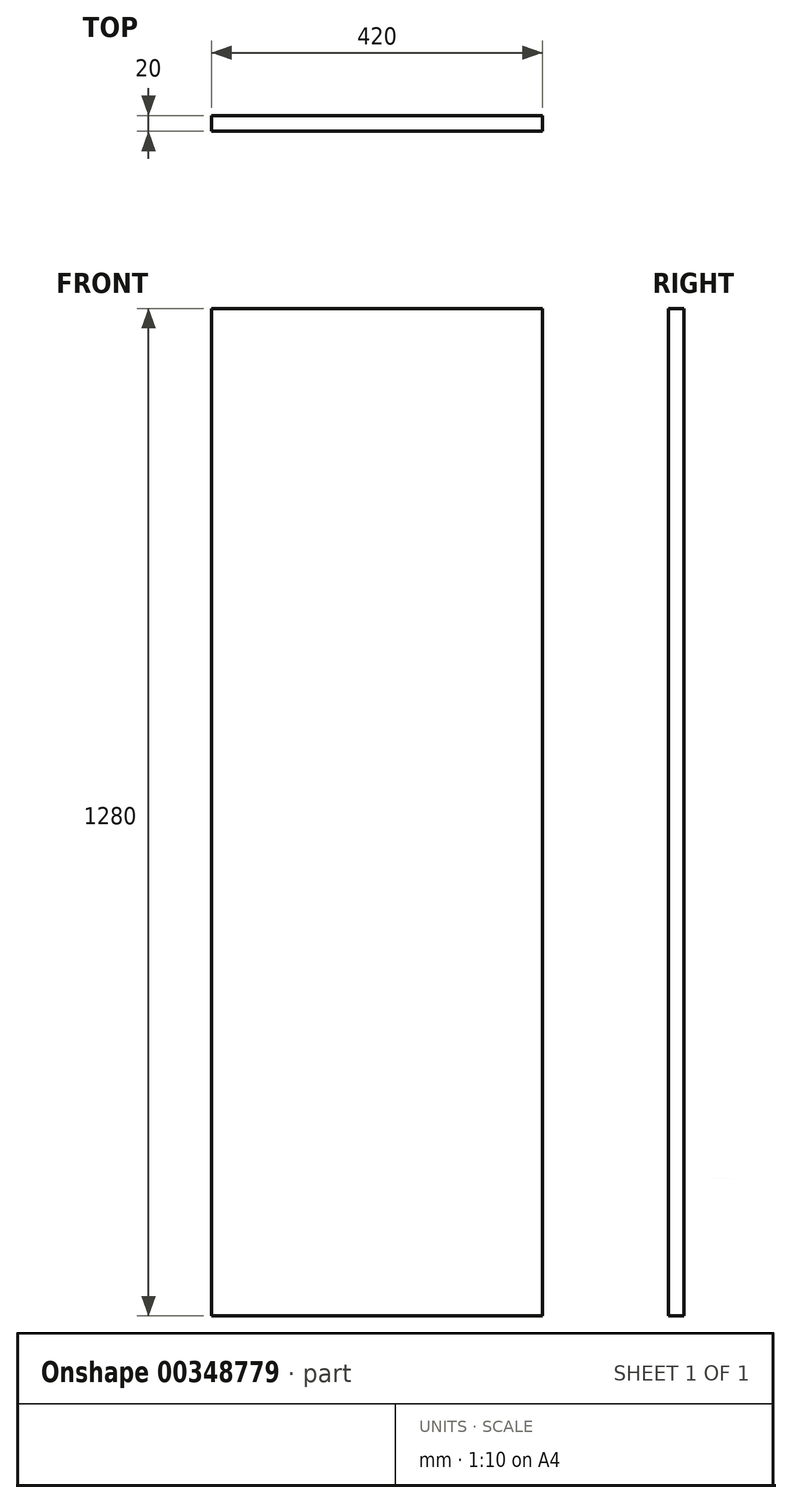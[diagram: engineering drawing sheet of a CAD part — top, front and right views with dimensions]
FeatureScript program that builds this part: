
annotation { "Feature Type Name" : "Feature", "Feature Type Description" : "" }
export const myFeature = defineFeature(function(context is Context, id is Id, definition is map)
    precondition{}
    {
        {
            var Q0;
            Q0=qCreatedBy(makeId("Front.planeOp"),FACE);
            var sketch = newSketch(context, id + "F0", { "sketchPlane" : qUnion([Q0])});
            skLineSegment(sketch, "E0.bottom", {"start": v(-420, -1280) * mm, "end": v(0, -1280) * mm});
            skLineSegment(sketch, "E0.top", {"start": v(-420, 0) * mm, "end": v(0, 0) * mm});
            skLineSegment(sketch, "E0.left", {"start": v(-420, -1280) * mm, "end": v(-420, 0) * mm});
            skLineSegment(sketch, "E0.right", {"start": v(0, -1280) * mm, "end": v(0, 0) * mm});
            skSolve(sketch);
        }
        {
            var Q0;
            Q0=qSketchRegion(id+"F0",true);
            extrude(context, id + "F1", {"entities" : qUnion([Q0]), "depth" : 20 * mm});
        }
    });
